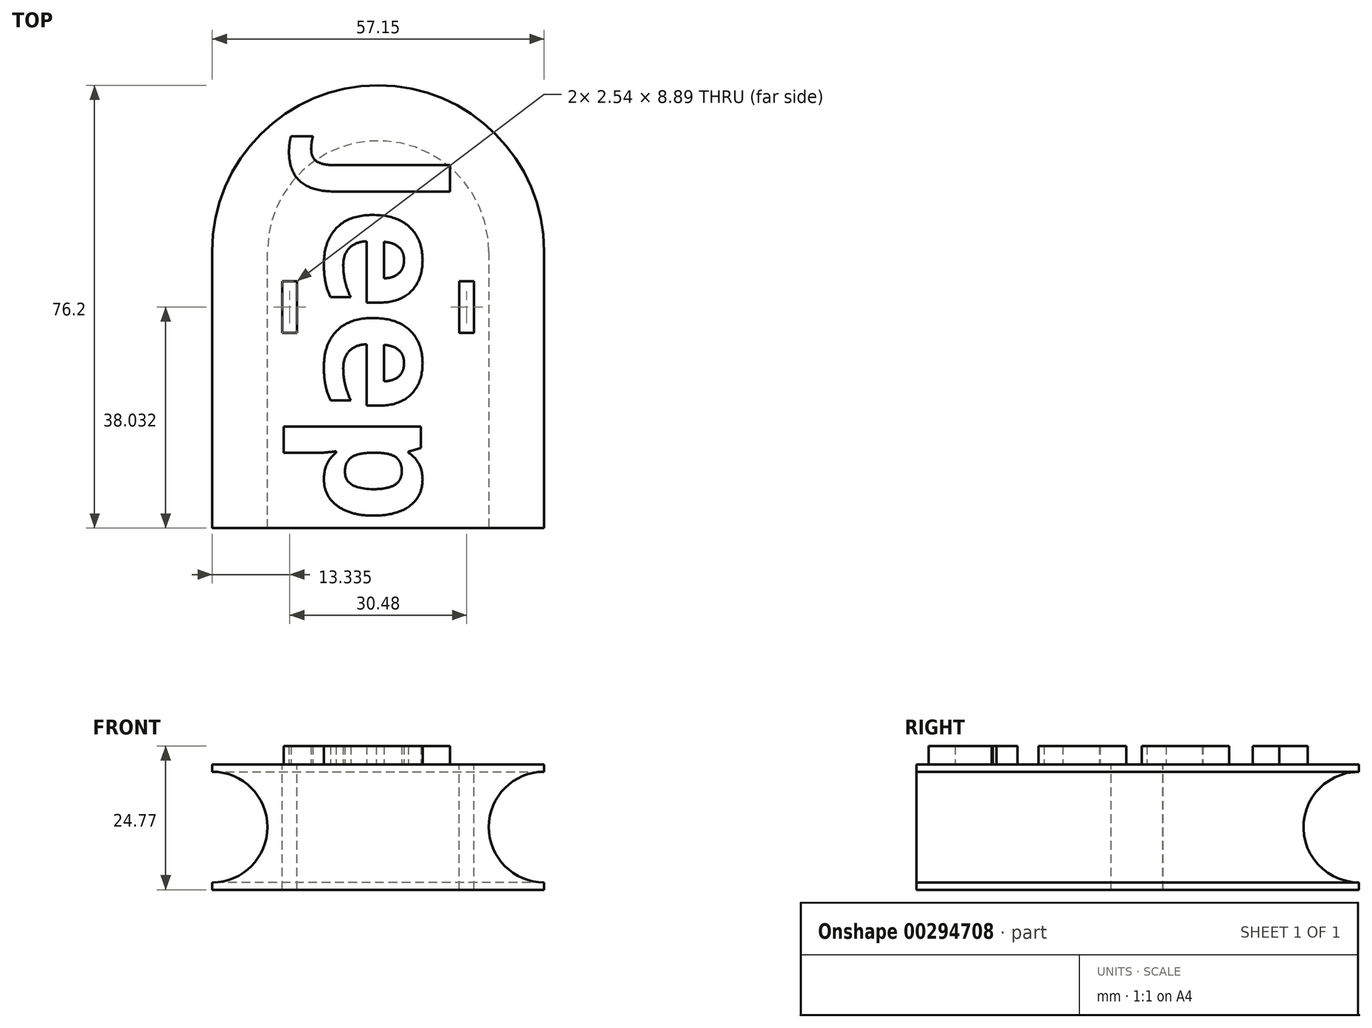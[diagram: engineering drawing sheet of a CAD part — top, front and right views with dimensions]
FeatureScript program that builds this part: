
annotation { "Feature Type Name" : "Feature", "Feature Type Description" : "" }
export const myFeature = defineFeature(function(context is Context, id is Id, definition is map)
    precondition{}
    {
        {
            var Q0;
            Q0=qCreatedBy(makeId("Top.planeOp"),FACE);
            var sketch = newSketch(context, id + "F0", { "sketchPlane" : qUnion([Q0])});
            skLineSegment(sketch, "E0.bottom", {"start": v(0, 0) * mm, "end": v(57.15, 0) * mm});
            skLineSegment(sketch, "E0.left", {"start": v(0, 0) * mm, "end": v(0, 47.62) * mm});
            skLineSegment(sketch, "E0.right", {"start": v(57.15, 0) * mm, "end": v(57.15, 47.62) * mm});
            skArc(sketch, "E1", {"start": v(57.15, 47.62) * mm, "mid": v(28.58, 76.2) * mm, "end": v(0, 47.63) * mm});
            skSolve(sketch);
        }
        {
            var Q0;
            Q0=makeQuery(id+"F0.imprint","IMPRINT",FACE,{"disambiguationData":[TD([[makeQuery(id+"F0.imprint","IMPRINT",EDGE,{"derivedFrom":sQuery(id+"F0.wireOp",EDGE,"E0.bottom")}),1.0]])]});
            extrude(context, id + "F1", {"entities" : qUnion([Q0]), "depth" : 21.59 * mm});
        }
        {
            var Q0;
            Q0=qCreatedBy(makeId("Front.planeOp"),FACE);
            var sketch = newSketch(context, id + "F2", { "sketchPlane" : qUnion([Q0])});
            skCircle(sketch, "E2", {"center": v(0, 10.8) * mm, "radius": 9.53 * mm});
            skSolve(sketch);
        }
        {
            var Q0;
            Q0=makeQuery(id+"F2.imprint","IMPRINT",FACE,{"disambiguationData":[TD([[makeQuery(id+"F2.imprint","IMPRINT",EDGE,{"derivedFrom":sQuery(id+"F2.wireOp",EDGE,"E2")}),1.0]])]});
            var Q1;
            Q1=makeQuery(id+"F1.opExtrude","CAP_EDGE",EDGE,{"disambiguationData":[OSD([sQuery(id+"F0.wireOp",EDGE,"E0.left")])],"isStart":false});
            var Q2;
            Q2=makeQuery(id+"F1.opExtrude","CAP_EDGE",EDGE,{"disambiguationData":[OSD([sQuery(id+"F0.wireOp",EDGE,"E1")])],"isStart":false});
            var Q3;
            Q3=makeQuery(id+"F1.opExtrude","CAP_EDGE",EDGE,{"disambiguationData":[OSD([sQuery(id+"F0.wireOp",EDGE,"E0.right")])],"isStart":false});
            sweep(context, id + "F3", {"operationType" : NewBodyOperationType.REMOVE, "profiles" : qUnion([Q0]), "path" : qUnion([Q1, Q2, Q3])});
        }
        {
            var Q0;
            Q0=makeQuery(id+"F1.opExtrude","CAP_FACE",FACE,{"disambiguationData":[OSD([sQuery(id+"F0.wireOp",EDGE,"E0.bottom"),sQuery(id+"F0.wireOp",EDGE,"E0.left"),sQuery(id+"F0.wireOp",EDGE,"E0.right"),sQuery(id+"F0.wireOp",EDGE,"E1")])],"isStart":false});
            var sketch = newSketch(context, id + "F4", { "sketchPlane" : qUnion([Q0])});
            skText(sketch, "E3", { "text": "Jeep", "fontName": "OpenSans-Bold.ttf"});
            const initialGuessF4  = {"E3": [0.01953, 0.06518, 0, -1, 0.02161]};
            skSetInitialGuess(sketch, initialGuessF4);
            skSolve(sketch);
        }
        {
            var Q0;
            Q0 = qSketchRegion(id + "F4", true);
            extrude(context, id + "F5", {"entities" : qUnion([Q0]), "operationType" : NewBodyOperationType.ADD, "depth" : 3.17 * mm});
        }
        {
            var Q0;
            {var subQ0=sQuery(id+"F0.wireOp",EDGE,"E0.right");var subQ1=sQuery(id+"F0.wireOp",EDGE,"E0.bottom");var subQ2=sQuery(id+"F0.wireOp",EDGE,"E1");var subQ3=sQuery(id+"F0.wireOp",EDGE,"E0.left");Q0=makeQuery(id+"F5.boolean.opBoolean","SPLIT",FACE,{"disambiguationData":[TD([makeQuery(id+"F1.opExtrude","SWEPT_FACE",FACE,{"disambiguationData":[OSD([subQ1])]})])],"derivedFrom":makeQuery(id+"F1.opExtrude","CAP_FACE",FACE,{"disambiguationData":[OSD([subQ1,subQ3,subQ0,subQ2])],"isStart":false})});}
            var sketch = newSketch(context, id + "F6", { "sketchPlane" : qUnion([Q0])});
            skLineSegment(sketch, "E4.bottom", {"start": v(45.08, 42.47) * mm, "end": v(42.54, 42.47) * mm});
            skLineSegment(sketch, "E4.top", {"start": v(45.08, 33.58) * mm, "end": v(42.54, 33.58) * mm});
            skLineSegment(sketch, "E4.left", {"start": v(45.08, 42.47) * mm, "end": v(45.08, 33.58) * mm});
            skLineSegment(sketch, "E4.right", {"start": v(42.54, 42.47) * mm, "end": v(42.54, 33.58) * mm});
            skLineSegment(sketch, "E5.bottom", {"start": v(14.6, 42.48) * mm, "end": v(12.06, 42.48) * mm});
            skLineSegment(sketch, "E5.top", {"start": v(14.6, 33.59) * mm, "end": v(12.06, 33.59) * mm});
            skLineSegment(sketch, "E5.left", {"start": v(14.6, 42.48) * mm, "end": v(14.6, 33.59) * mm});
            skLineSegment(sketch, "E5.right", {"start": v(12.06, 42.48) * mm, "end": v(12.06, 33.59) * mm});
            skSolve(sketch);
        }
        {
            var Q0;
            Q0=makeQuery(id+"F6.imprint","IMPRINT",FACE,{"disambiguationData":[TD([[makeQuery(id+"F6.imprint","IMPRINT",EDGE,{"derivedFrom":sQuery(id+"F6.wireOp",EDGE,"E5.bottom")}),1.0]])]});
            var Q1;
            Q1=makeQuery(id+"F6.imprint","IMPRINT",FACE,{"disambiguationData":[TD([[makeQuery(id+"F6.imprint","IMPRINT",EDGE,{"derivedFrom":sQuery(id+"F6.wireOp",EDGE,"E4.bottom")}),1.0]])]});
            extrude(context, id + "F7", {"entities" : qUnion([Q0, Q1]), "operationType" : NewBodyOperationType.REMOVE, "oppositeDirection" : true, "depth" : 25.4 * mm});
        }
    });
